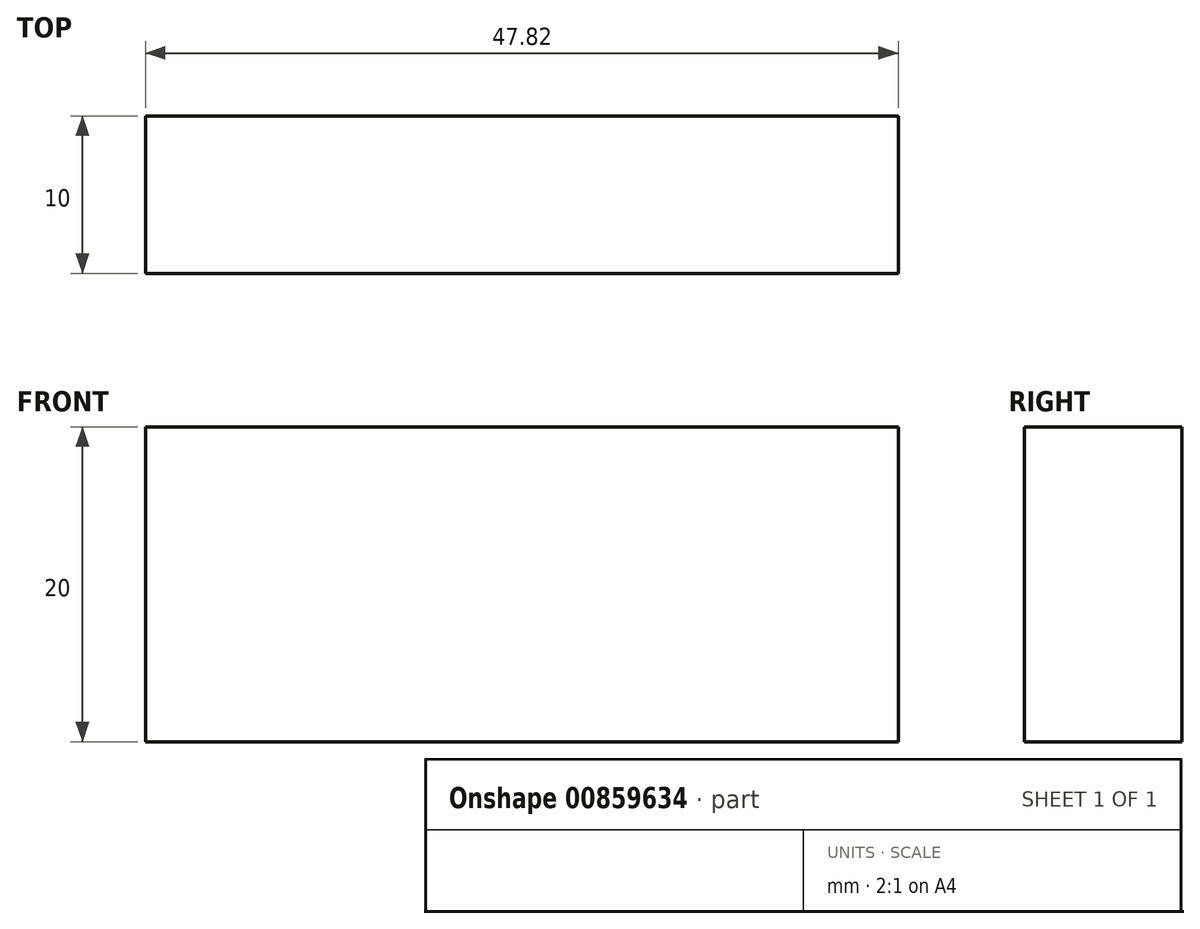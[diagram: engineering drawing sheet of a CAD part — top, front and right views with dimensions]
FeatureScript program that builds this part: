
annotation { "Feature Type Name" : "Feature", "Feature Type Description" : "" }
export const myFeature = defineFeature(function(context is Context, id is Id, definition is map)
    precondition{}
    {
        {
            var Q0;
            Q0=qCreatedBy(makeId("Front.planeOp"),FACE);
            var sketch = newSketch(context, id + "F0", { "sketchPlane" : qUnion([Q0])});
            skLineSegment(sketch, "E0.bottom", {"start": v(23.9, 10) * mm, "end": v(-23.9, 10) * mm});
            skLineSegment(sketch, "E0.top", {"start": v(23.9, -10) * mm, "end": v(-23.9, -10) * mm});
            skLineSegment(sketch, "E0.left", {"start": v(23.9, 10) * mm, "end": v(23.9, -10) * mm});
            skLineSegment(sketch, "E0.right", {"start": v(-23.9, 10) * mm, "end": v(-23.9, -10) * mm});
            skPoint(sketch, "E0.middle", {"position": v(0, 0) * mm});
            skPoint(sketch, "E1", {"position": v(-23.9, 0) * mm});
            skSolve(sketch);
        }
        {
            var Q0;
            Q0=makeQuery(id+"F0.imprint","IMPRINT",FACE,{"disambiguationData":[TD([[makeQuery(id+"F0.imprint","IMPRINT",EDGE,{"derivedFrom":sQuery(id+"F0.wireOp",EDGE,"E0.bottom")}),1.0]])]});
            extrude(context, id + "F1", {"entities" : qUnion([Q0]), "endBound" : BoundingType.SYMMETRIC, "depth" : 10 * mm, "offsetDistance" : 25 * mm});
        }
    });
